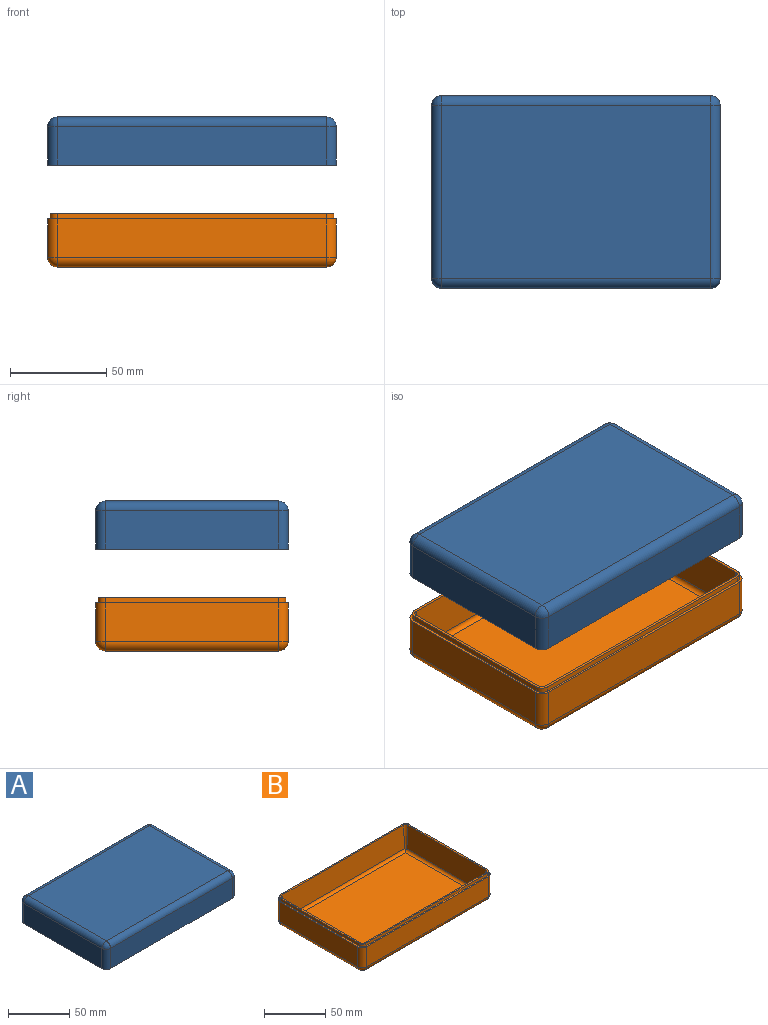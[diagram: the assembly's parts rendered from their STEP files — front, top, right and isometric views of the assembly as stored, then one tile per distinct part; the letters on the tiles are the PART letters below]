
ASSEMBLY  parts=2 mates=1
PART A: 40 faces, bbox 150x100x25 mm
  f0: cylinder r=2.5mm len=92.14mm, axis (0,1,0), area 344mm2, adj f1,f2,f3,f7,f35,f36
  f1: cone r=2.5mm half-angle=3deg, axis (0,0,-1), area 57.6mm2, adj f0,f3,f33,f36,f39
  f2: cone r=2.5mm half-angle=3deg, axis (0,0,-1), area 57.6mm2, adj f0,f7,f33,f36,f37
  f3: cylinder r=2.5mm len=142.14mm, axis (-1,0,0), area 533.8mm2, adj f0,f1,f4,f5,f35,f39
  f4: cone r=2.5mm half-angle=3deg, axis (0,0,-1), area 57.6mm2, adj f3,f5,f33,f38,f39
  f5: cylinder r=2.5mm len=92.14mm, axis (0,1,0), area 344mm2, adj f3,f4,f6,f7,f35,f38
  f6: cone r=2.5mm half-angle=3deg, axis (0,0,-1), area 57.6mm2, adj f5,f7,f33,f37,f38
  f7: cylinder r=2.5mm len=142.14mm, axis (-1,0,0), area 533.8mm2, adj f0,f2,f5,f6,f35,f37
  f8: plane 150x100mm, normal (0,0,-1), area 609.4mm2, adj f9,f10,f11,f12,f14,f18,f19,f25
  f9: plane 140x20mm, normal (0,-1,0), area 2800mm2, adj f8,f19,f22,f25
  f10: plane 90x20mm, normal (1,0,0), area 1800mm2, adj f8,f18,f23,f25
  f11: plane 140x20mm, normal (0,1,0), area 2800mm2, adj f8,f14,f17,f18
  f12: plane 90x20mm, normal (-1,0,0), area 1800mm2, adj f8,f14,f16,f19
  f13: plane 140x90mm, normal (0,0,1), area 12600mm2, adj f16,f17,f22,f23
  f14: cylinder r=5mm len=20mm, axis (0,0,1), area 157.1mm2, adj f8,f11,f12,f15
  f15: sphere r=5mm, area 39.3mm2, adj f14,f16,f17
  f16: cylinder r=5mm len=90mm, axis (0,1,0), area 706.9mm2, adj f12,f13,f15,f20
  f17: cylinder r=5mm len=140mm, axis (1,0,0), area 1099.6mm2, adj f11,f13,f15,f21
  f18: cylinder r=5mm len=20mm, axis (0,0,-1), area 157.1mm2, adj f8,f10,f11,f21
  f19: cylinder r=5mm len=20mm, axis (0,0,-1), area 157.1mm2, adj f8,f9,f12,f20
  f20: sphere r=5mm, area 39.3mm2, adj f16,f19,f22
  f21: sphere r=5mm, area 39.3mm2, adj f17,f18,f23
  f22: cylinder r=5mm len=140mm, axis (-1,0,0), area 1099.6mm2, adj f9,f13,f20,f24
  f23: cylinder r=5mm len=90mm, axis (0,-1,0), area 706.9mm2, adj f10,f13,f21,f24
  f24: sphere r=5mm, area 39.3mm2, adj f22,f23,f25
  f25: cylinder r=5mm len=20mm, axis (0,0,1), area 157.1mm2, adj f8,f9,f10,f24
  f26: cylinder r=3.75mm len=3.75mm, axis (0,0,-1), area 16.2mm2, adj f8,f27,f33,f34
  f27: plane 90x2.75mm, normal (1,0,0), area 247.5mm2, adj f8,f26,f28,f33
  f28: cylinder r=3.75mm len=3.75mm, axis (0,0,-1), area 16.2mm2, adj f8,f27,f29,f33
  f29: plane 140x2.75mm, normal (0,1,0), area 385mm2, adj f8,f28,f30,f33
  f30: cylinder r=3.75mm len=3.75mm, axis (0,0,-1), area 16.2mm2, adj f8,f29,f31,f33
  f31: plane 90x2.75mm, normal (-1,0,0), area 247.5mm2, adj f8,f30,f32,f33
  f32: cylinder r=3.75mm len=3.75mm, axis (0,0,-1), area 16.2mm2, adj f8,f31,f33,f34
  f33: plane 147.5x97.5mm, normal (0,0,-1), area 599.5mm2, adj f1,f2,f4,f6,f26,f27,f28,f29
  f34: plane 140x2.75mm, normal (0,-1,0), area 385mm2, adj f8,f26,f32,f33
  f35: plane 138.19x88.19mm, normal (0,0,-1), area 12185.9mm2, adj f0,f3,f5,f7
  f36: plane 90x17.38mm, normal (1,0,-0.05), area 1566.4mm2, adj f0,f1,f2,f33
  f37: plane 140x17.38mm, normal (0,-1,-0.05), area 2436.7mm2, adj f2,f6,f7,f33
  f38: plane 90x17.38mm, normal (-1,0,-0.05), area 1566.4mm2, adj f4,f5,f6,f33
  f39: plane 140x17.38mm, normal (0,1,-0.05), area 2436.7mm2, adj f1,f3,f4,f33
PART B: 40 faces, bbox 150x100x27.8 mm
  f0: cylinder r=2.5mm len=91.75mm, axis (0,-1,0), area 342.5mm2, adj f1,f2,f3,f7,f35,f37
  f1: cone r=2.5mm half-angle=3deg, axis (0,0,1), area 69.7mm2, adj f0,f3,f33,f36,f37
  f2: cone r=2.5mm half-angle=3deg, axis (0,0,1), area 69.7mm2, adj f0,f7,f33,f37,f38
  f3: cylinder r=2.5mm len=141.75mm, axis (1,0,0), area 532.3mm2, adj f0,f1,f4,f5,f35,f36
  f4: cone r=2.5mm half-angle=3deg, axis (0,0,1), area 69.7mm2, adj f3,f5,f33,f36,f39
  f5: cylinder r=2.5mm len=91.75mm, axis (0,-1,0), area 342.5mm2, adj f3,f4,f6,f7,f35,f39
  f6: cone r=2.5mm half-angle=3deg, axis (0,0,1), area 69.7mm2, adj f5,f7,f33,f38,f39
  f7: cylinder r=2.5mm len=141.75mm, axis (1,0,0), area 532.3mm2, adj f0,f2,f5,f6,f35,f38
  f8: plane 150x100mm, normal (0,0,1), area 609.4mm2, adj f18,f19,f20,f21,f22,f23,f24,f25
  f9: plane 140x90mm, normal (0,0,-1), area 12600mm2, adj f10,f11,f12,f13
  f10: cylinder r=5mm len=140mm, axis (1,0,0), area 1099.6mm2, adj f9,f16,f17,f25
  f11: cylinder r=5mm len=90mm, axis (0,1,0), area 706.9mm2, adj f9,f15,f17,f24
  f12: cylinder r=5mm len=140mm, axis (-1,0,0), area 1099.6mm2, adj f9,f14,f15,f22
  f13: cylinder r=5mm len=90mm, axis (0,-1,0), area 706.9mm2, adj f9,f14,f16,f20
  f14: sphere r=5mm, area 39.3mm2, adj f12,f13,f18
  f15: sphere r=5mm, area 39.3mm2, adj f11,f12,f21
  f16: sphere r=5mm, area 39.3mm2, adj f10,f13,f19
  f17: sphere r=5mm, area 39.3mm2, adj f10,f11,f23
  f18: cylinder r=5mm len=20mm, axis (0,0,1), area 157.1mm2, adj f8,f14,f20,f22
  f19: cylinder r=5mm len=20mm, axis (0,0,-1), area 157.1mm2, adj f8,f16,f20,f25
  f20: plane 90x20mm, normal (-1,0,0), area 1800mm2, adj f8,f13,f18,f19
  f21: cylinder r=5mm len=20mm, axis (0,0,-1), area 157.1mm2, adj f8,f15,f22,f24
  f22: plane 140x20mm, normal (0,1,0), area 2800mm2, adj f8,f12,f18,f21
  f23: cylinder r=5mm len=20mm, axis (0,0,1), area 157.1mm2, adj f8,f17,f24,f25
  f24: plane 90x20mm, normal (1,0,0), area 1800mm2, adj f8,f11,f21,f23
  f25: plane 140x20mm, normal (0,-1,0), area 2800mm2, adj f8,f10,f19,f23
  f26: cylinder r=3.75mm len=3.75mm, axis (0,0,-1), area 16.2mm2, adj f8,f27,f33,f34
  f27: plane 90x2.75mm, normal (-1,0,0), area 247.5mm2, adj f8,f26,f28,f33
  f28: cylinder r=3.75mm len=3.75mm, axis (0,0,-1), area 16.2mm2, adj f8,f27,f29,f33
  f29: plane 140x2.75mm, normal (0,-1,0), area 385mm2, adj f8,f28,f30,f33
  f30: cylinder r=3.75mm len=3.75mm, axis (0,0,-1), area 16.2mm2, adj f8,f29,f31,f33
  f31: plane 90x2.75mm, normal (1,0,0), area 247.5mm2, adj f8,f30,f32,f33
  f32: cylinder r=3.75mm len=3.75mm, axis (0,0,-1), area 16.2mm2, adj f8,f31,f33,f34
  f33: plane 147.5x97.5mm, normal (0,0,1), area 599.5mm2, adj f1,f2,f4,f6,f26,f27,f28,f29
  f34: plane 140x2.75mm, normal (0,1,0), area 385mm2, adj f8,f26,f32,f33
  f35: plane 137.61x87.61mm, normal (0,0,1), area 12055.7mm2, adj f0,f3,f5,f7
  f36: plane 140x22.88mm, normal (0,1,0.05), area 3207.7mm2, adj f1,f3,f4,f33
  f37: plane 90x22.88mm, normal (-1,0,0.05), area 2062.1mm2, adj f0,f1,f2,f33
  f38: plane 140x22.88mm, normal (0,-1,0.05), area 3207.7mm2, adj f2,f6,f7,f33
  f39: plane 90x22.88mm, normal (1,0,0.05), area 2062.1mm2, adj f4,f5,f6,f33
PLACE A t=(-1.24,-20.79,-38.99)mm
PLACE B t=(-1.24,-20.79,-66.99)mm
MATE planar A.f10 <-> B.f24  axis (1,0,0) through (73.76,-20.79,-28.99)mm
